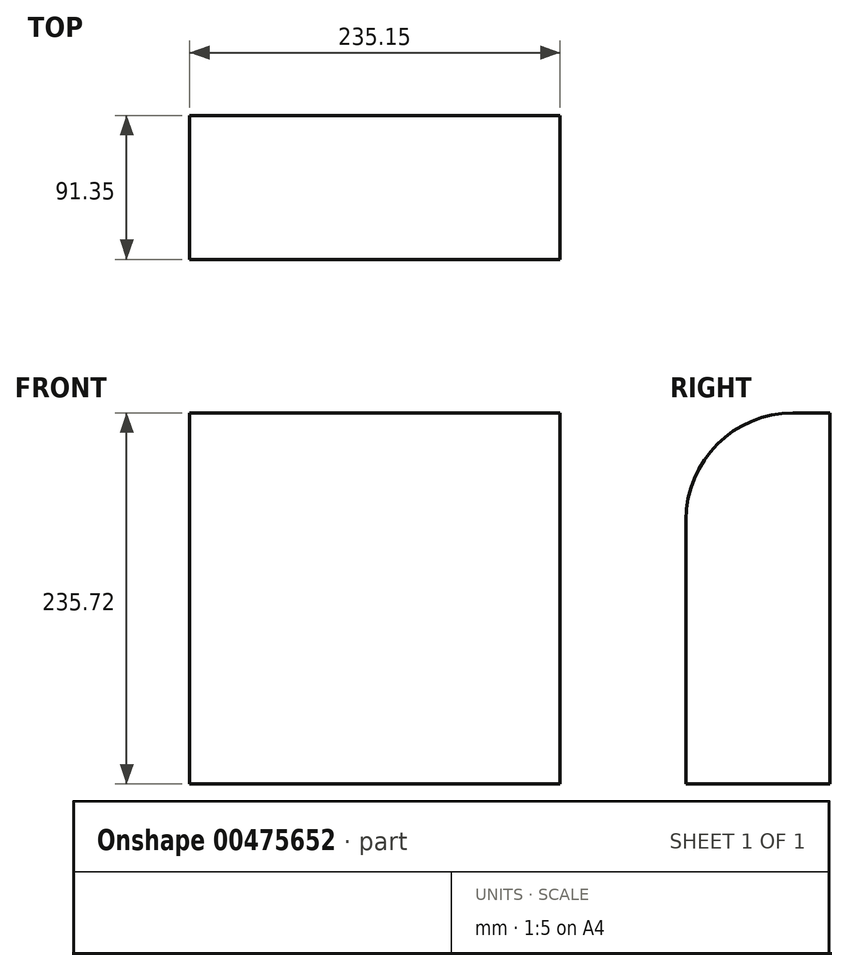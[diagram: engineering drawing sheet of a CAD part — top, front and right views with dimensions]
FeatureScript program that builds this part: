
annotation { "Feature Type Name" : "Feature", "Feature Type Description" : "" }
export const myFeature = defineFeature(function(context is Context, id is Id, definition is map)
    precondition{}
    {
        {
            var Q0;
            Q0=qCreatedBy(makeId("Top.planeOp"),FACE);
            var sketch = newSketch(context, id + "F0", { "sketchPlane" : qUnion([Q0])});
            skLineSegment(sketch, "E0.bottom", {"start": v(-110.77, 38.28) * mm, "end": v(124.38, 38.28) * mm});
            skLineSegment(sketch, "E0.top", {"start": v(-110.77, -53.07) * mm, "end": v(124.38, -53.07) * mm});
            skLineSegment(sketch, "E0.left", {"start": v(-110.77, 38.28) * mm, "end": v(-110.77, -53.07) * mm});
            skLineSegment(sketch, "E0.right", {"start": v(124.38, 38.28) * mm, "end": v(124.38, -53.07) * mm});
            skSolve(sketch);
        }
        {
            var Q0;
            Q0=makeQuery(id+"F0.imprint","IMPRINT",FACE,{"disambiguationData":[TD([[makeQuery(id+"F0.imprint","IMPRINT",EDGE,{"derivedFrom":sQuery(id+"F0.wireOp",EDGE,"E0.bottom")}),-1.0]])]});
            var Q1;
            Q1=sQuery(id+"F0.wireOp",EDGE,"E0.top");
            extrude(context, id + "F1", {"entities" : qUnion([Q0]), "surfaceEntities" : qUnion([Q1]), "depth" : 119.13 * mm, "hasSecondDirection" : true, "secondDirectionOppositeDirection" : true, "secondDirectionDepth" : 116.6 * mm});
        }
        {
            var Q0;
            Q0=makeQuery(id+"F1.opExtrude","CAP_EDGE",EDGE,{"disambiguationData":[OSD([sQuery(id+"F0.wireOp",EDGE,"E0.top")])],"isStart":false});
            fillet(context, id + "F2", {"entities" : qUnion([Q0]), "radius" : 68.07 * mm, "tangentPropagation" : true, "allowEdgeOverflow" : false});
        }
    });
